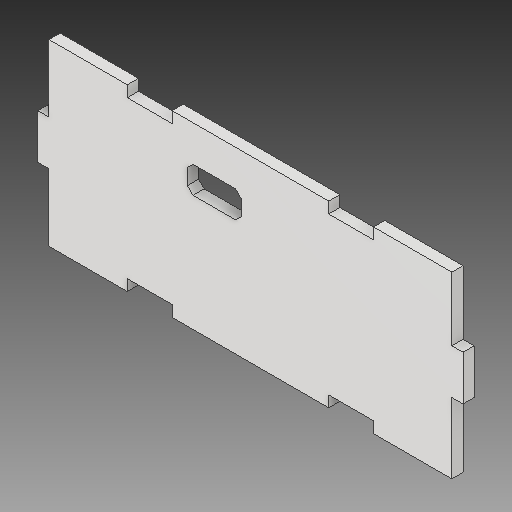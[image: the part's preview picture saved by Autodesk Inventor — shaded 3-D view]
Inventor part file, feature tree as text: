
AUTODESK INVENTOR PART (.ipt)
format: ipt  version: 2018.2 (Build 222227000, 227)  size: 124,416 bytes
history: native  units: in
note: dims shown in document units (in); Inventor stores cm internally (conversion verified against a paired STEP export)
features: other x3, reference x2, extrude x1, sketch x1
ambient origin geometry x8: Origin, YZ Plane, XZ Plane, XY Plane, X Axis, Y Axis, Z Axis, Center Point
bodies: Solid1 (feature_tree)
feature tree (7):
  extrude  "Extrusion1"  [1 undecoded]
  sketch  "Sketch1"  dims[d0=0.125in d1=0.0in]
  reference  "Reference2"
  reference  "Reference5"
  other  "Assembly1.iam"
  other  "Face:1"
  other  "Side 2:1"
note: 1 required parameter value undecoded (feature->parameter linkage not recoverable at this tier; creation-order binding heuristic only, values carry confidence <= 0.55)
